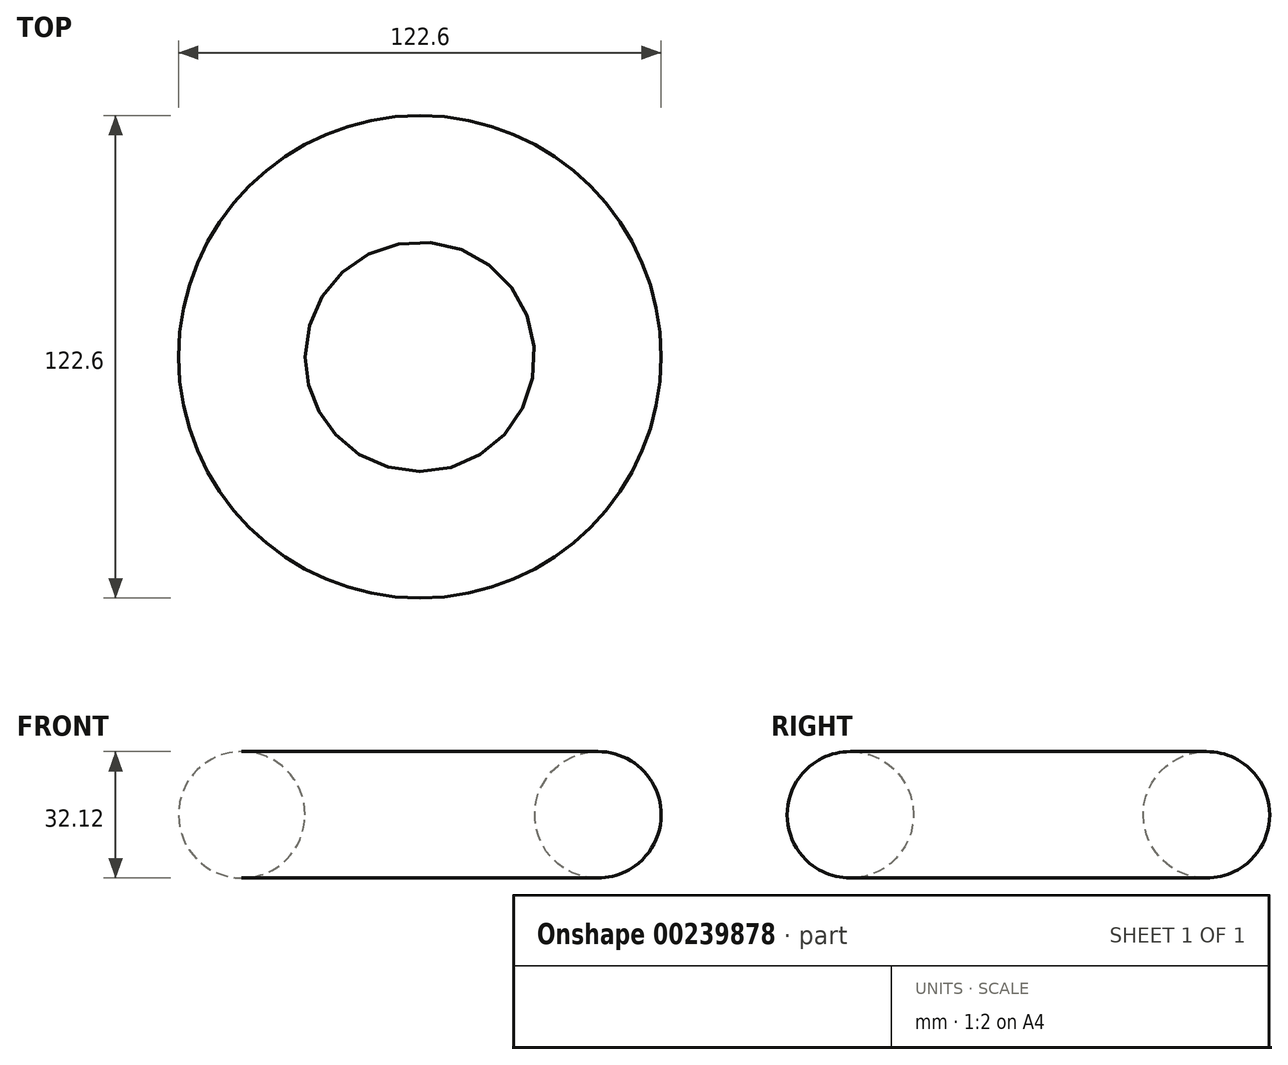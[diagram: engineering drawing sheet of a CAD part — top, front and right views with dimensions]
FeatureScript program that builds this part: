
annotation { "Feature Type Name" : "Feature", "Feature Type Description" : "" }
export const myFeature = defineFeature(function(context is Context, id is Id, definition is map)
    precondition{}
    {
        {
            var Q0;
            Q0=qCreatedBy(makeId("Front.planeOp"),FACE);
            var sketch = newSketch(context, id + "F0", { "sketchPlane" : qUnion([Q0])});
            skCircle(sketch, "E0", {"center": v(-45.24, 0) * mm, "radius": 16.06 * mm});
            skSolve(sketch);
        }
        {
            var Q0;
            Q0=qCreatedBy(makeId("Front.planeOp"),FACE);
            var sketch = newSketch(context, id + "F1", { "sketchPlane" : qUnion([Q0])});
            skLineSegment(sketch, "E1", {"start": v(0, 17.45) * mm, "end": v(0, -16.65) * mm, "construction": true});
            skSolve(sketch);
        }
        {
            var Q0;
            Q0=sQuery(id+"F0.wireOp",EDGE,"E0");
            var Q1;
            Q1=sQuery(id+"F1.wireOp",EDGE,"E1");
            revolve(context, id + "F2", {"bodyType" : ToolBodyType.SURFACE, "surfaceEntities" : qUnion([Q0]), "axis" : qUnion([Q1]), "revolveType" : RevolveType.FULL});
        }
    });
